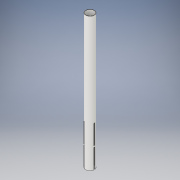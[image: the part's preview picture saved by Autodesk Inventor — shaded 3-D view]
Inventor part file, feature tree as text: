
AUTODESK INVENTOR PART (.ipt)
format: ipt  version: 2018 (Build 220112000, 112)  size: 137,216 bytes
history: native  units: in
note: dims shown in document units (in); Inventor stores cm internally (conversion verified against a paired STEP export)
features: extrude x2, sketch x2, pattern_circular x1, projected_geometry x1
ambient origin geometry x8: Origin, YZ Plane, XZ Plane, XY Plane, X Axis, Y Axis, Z Axis, Center Point
bodies: Solid1 (feature_tree)
feature tree (6):
  extrude  "Extrusion1"  Depth=3.125in
  extrude  "Extrusion2"  Depth=7.0in
  pattern_circular  "Circular Pattern1"  [2 undecoded]
  sketch  "Sketch1"  dims[d0=2.875in d1=3.125in]
  sketch  "Sketch2"  dims[d2=48.0in d3=0.0in d4=7.0in d5=0.375in d6=1.375in d7=3.0in d8=0.0in d9=1.1811in d10=360.0deg d12=7.0in d13=0.375in d14=0.5in]
  projected_geometry  "Projected Loop1"
note: 2 required parameter values undecoded (feature->parameter linkage not recoverable at this tier; creation-order binding heuristic only, values carry confidence <= 0.55)
